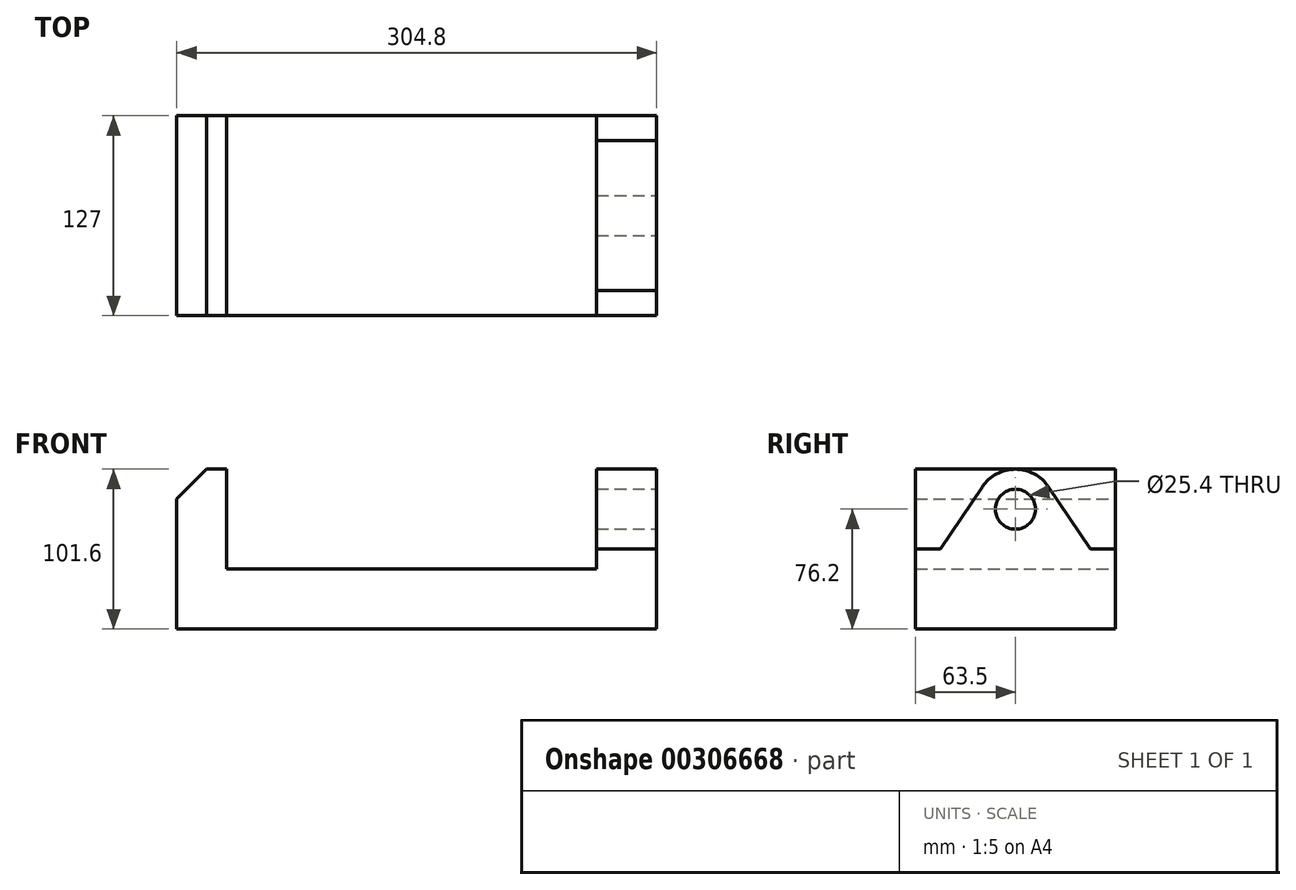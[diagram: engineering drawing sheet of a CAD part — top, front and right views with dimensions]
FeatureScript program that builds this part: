
annotation { "Feature Type Name" : "Feature", "Feature Type Description" : "" }
export const myFeature = defineFeature(function(context is Context, id is Id, definition is map)
    precondition{}
    {
        {
            var Q0;
            Q0=qCreatedBy(makeId("Front.planeOp"),FACE);
            var sketch = newSketch(context, id + "F0", { "sketchPlane" : qUnion([Q0])});
            skLineSegment(sketch, "E0", {"start": v(0, 0) * mm, "end": v(0, 101.6) * mm});
            skLineSegment(sketch, "E1", {"start": v(0, 101.6) * mm, "end": v(31.75, 101.6) * mm});
            skLineSegment(sketch, "E2", {"start": v(31.75, 101.6) * mm, "end": v(31.75, 38.1) * mm});
            skLineSegment(sketch, "E3", {"start": v(31.75, 38.1) * mm, "end": v(266.7, 38.1) * mm});
            skLineSegment(sketch, "E4", {"start": v(266.7, 38.1) * mm, "end": v(266.7, 101.6) * mm});
            skLineSegment(sketch, "E5", {"start": v(266.7, 101.6) * mm, "end": v(304.8, 101.6) * mm});
            skLineSegment(sketch, "E6", {"start": v(304.8, 101.6) * mm, "end": v(304.8, 0) * mm});
            skLineSegment(sketch, "E7", {"start": v(304.8, 0) * mm, "end": v(0, 0) * mm});
            skSolve(sketch);
        }
        {
            var Q0;
            Q0=makeQuery(id+"F0.imprint","IMPRINT",FACE,{"disambiguationData":[TD([[makeQuery(id+"F0.imprint","IMPRINT",EDGE,{"derivedFrom":sQuery(id+"F0.wireOp",EDGE,"E0")}),-1.0]])]});
            extrude(context, id + "F1", {"entities" : qUnion([Q0]), "endBound" : BoundingType.SYMMETRIC, "depth" : 127 * mm});
        }
        {
            var Q0;
            Q0=makeQuery(id+"F1.opExtrude","SWEPT_FACE",FACE,{"disambiguationData":[OSD([sQuery(id+"F0.wireOp",EDGE,"E6")])]});
            var sketch = newSketch(context, id + "F2", { "sketchPlane" : qUnion([Q0])});
            skLineSegment(sketch, "E8.0.0", {"start": v(63.5, 0) * mm, "end": v(63.5, 101.6) * mm});
            skLineSegment(sketch, "E8.0.1", {"start": v(63.5, 101.6) * mm, "end": v(-63.5, 101.6) * mm});
            skLineSegment(sketch, "E8.0.2", {"start": v(-63.5, 101.6) * mm, "end": v(-63.5, 0) * mm});
            skLineSegment(sketch, "E8.0.3", {"start": v(-63.5, 0) * mm, "end": v(63.5, 0) * mm});
            skLineSegment(sketch, "E9", {"start": v(-63.5, 0) * mm, "end": v(-63.5, 50.8) * mm});
            skLineSegment(sketch, "E10", {"start": v(0, 0) * mm, "end": v(0, 101.6) * mm, "construction": true});
            skCircle(sketch, "E11", {"center": v(0, 76.2) * mm, "radius": 25.4 * mm});
            skLineSegment(sketch, "E12", {"start": v(-63.5, 50.8) * mm, "end": v(-47.62, 50.8) * mm});
            skLineSegment(sketch, "E13", {"start": v(-47.62, 50.8) * mm, "end": v(-21.1, 90.35) * mm});
            skLineSegment(sketch, "E14", {"start": v(63.5, 0) * mm, "end": v(63.5, 50.8) * mm});
            skLineSegment(sketch, "E15", {"start": v(63.5, 50.8) * mm, "end": v(47.62, 50.8) * mm});
            skLineSegment(sketch, "E16", {"start": v(47.62, 50.8) * mm, "end": v(21.1, 90.35) * mm});
            skSolve(sketch);
        }
        {
            var Q0;
            {var subQ4=sQuery(id+"F2.wireOp",EDGE,"E8.0.2");Q0=makeQuery(id+"F2.imprint","IMPRINT",FACE,{"disambiguationData":[TD([[makeQuery(id+"F2.imprint","IMPRINT",EDGE,{"derivedFrom":subQ4}),1.0]])]});}
            var Q1;
            {var subQ4=sQuery(id+"F2.wireOp",EDGE,"E8.0.0");Q1=makeQuery(id+"F2.imprint","IMPRINT",FACE,{"disambiguationData":[TD([[makeQuery(id+"F2.imprint","IMPRINT",EDGE,{"derivedFrom":subQ4}),-1.0]])]});}
            extrude(context, id + "F3", {"entities" : qUnion([Q0, Q1]), "operationType" : NewBodyOperationType.REMOVE, "oppositeDirection" : true, "depth" : 38.1 * mm});
        }
        {
            var Q0;
            Q0=makeQuery(id+"F1.opExtrude","SWEPT_FACE",FACE,{"disambiguationData":[OSD([sQuery(id+"F0.wireOp",EDGE,"E6")])]});
            var sketch = newSketch(context, id + "F4", { "sketchPlane" : qUnion([Q0])});
            skArc(sketch, "E17.0.0", {"start": v(21.1, 90.35) * mm, "mid": v(0, 101.6) * mm, "end": v(-21.1, 90.35) * mm});
            skLineSegment(sketch, "E17.0.1", {"start": v(-21.1, 90.35) * mm, "end": v(-47.63, 50.8) * mm});
            skLineSegment(sketch, "E17.0.2", {"start": v(-47.62, 50.8) * mm, "end": v(-63.5, 50.8) * mm});
            skLineSegment(sketch, "E17.0.3", {"start": v(-63.5, 50.8) * mm, "end": v(-63.5, 0) * mm});
            skLineSegment(sketch, "E17.0.4", {"start": v(-63.5, 0) * mm, "end": v(63.5, 0) * mm});
            skLineSegment(sketch, "E17.0.5", {"start": v(63.5, 0) * mm, "end": v(63.5, 50.8) * mm});
            skLineSegment(sketch, "E17.0.6", {"start": v(63.5, 50.8) * mm, "end": v(47.63, 50.8) * mm});
            skLineSegment(sketch, "E17.0.7", {"start": v(47.63, 50.8) * mm, "end": v(21.1, 90.35) * mm});
            skCircle(sketch, "E18", {"center": v(0, 76.2) * mm, "radius": 12.7 * mm});
            skLineSegment(sketch, "E19", {"start": v(0, 0) * mm, "end": v(-12.7, 0) * mm});
            skLineSegment(sketch, "E20", {"start": v(-12.7, 0) * mm, "end": v(-12.7, 16.51) * mm});
            skLineSegment(sketch, "E21", {"start": v(-12.7, 16.51) * mm, "end": v(-31.75, 16.51) * mm});
            skLineSegment(sketch, "E22", {"start": v(-31.75, 16.51) * mm, "end": v(-31.75, 29.21) * mm});
            skLineSegment(sketch, "E23", {"start": v(-31.75, 29.21) * mm, "end": v(-12.7, 29.21) * mm});
            skLineSegment(sketch, "E24", {"start": v(-12.7, 29.21) * mm, "end": v(-12.7, 38.1) * mm});
            skLineSegment(sketch, "E25", {"start": v(-12.7, 38.1) * mm, "end": v(0, 38.1) * mm});
            skLineSegment(sketch, "E26.MirrorCS", {"start": v(12.7, 0) * mm, "end": v(12.7, 16.51) * mm});
            skLineSegment(sketch, "E27.MirrorCS", {"start": v(12.7, 16.51) * mm, "end": v(31.75, 16.51) * mm});
            skLineSegment(sketch, "E28.MirrorCS", {"start": v(31.75, 16.51) * mm, "end": v(31.75, 29.21) * mm});
            skLineSegment(sketch, "E29.MirrorCS", {"start": v(31.75, 29.21) * mm, "end": v(12.7, 29.21) * mm});
            skLineSegment(sketch, "E30.MirrorCS", {"start": v(12.7, 38.1) * mm, "end": v(0, 38.1) * mm});
            skLineSegment(sketch, "E31.MirrorCS", {"start": v(12.7, 29.21) * mm, "end": v(12.7, 38.1) * mm});
            skLineSegment(sketch, "E32.MirrorCS", {"start": v(0, 0) * mm, "end": v(12.7, 0) * mm});
            skSolve(sketch);
        }
        {
            var Q0;
            Q0=makeQuery(id+"F4.imprint","IMPRINT",FACE,{"disambiguationData":[TD([[makeQuery(id+"F4.imprint","IMPRINT",EDGE,{"derivedFrom":sQuery(id+"F4.wireOp",EDGE,"E19")}),1.0]])]});
            var Q1;
            Q1=makeQuery(id+"F4.imprint","IMPRINT",FACE,{"disambiguationData":[TD([[makeQuery(id+"F4.imprint","IMPRINT",EDGE,{"derivedFrom":sQuery(id+"F4.wireOp",EDGE,"E18")}),1.0]])]});
            extrude(context, id + "F5", {"entities" : qUnion([Q0, Q1]), "operationType" : NewBodyOperationType.REMOVE, "oppositeDirection" : true, "depth" : 273.05 * mm});
        }
        {
            var Q0;
            Q0=makeQuery(id+"F1.opExtrude","SWEPT_EDGE",EDGE,{"disambiguationData":[OSD([sQuery(id+"F0.wireOp",EDGE,"E0"),sQuery(id+"F0.wireOp",EDGE,"E1")])]});
            chamfer(context, id + "F6", {"entities" : qUnion([Q0]), "chamferType" : ChamferType.TWO_OFFSETS, "width1" : 19.05 * mm, "oppositeDirection" : false, "width2" : 19.05 * mm, "tangentPropagation" : true});
        }
    });
